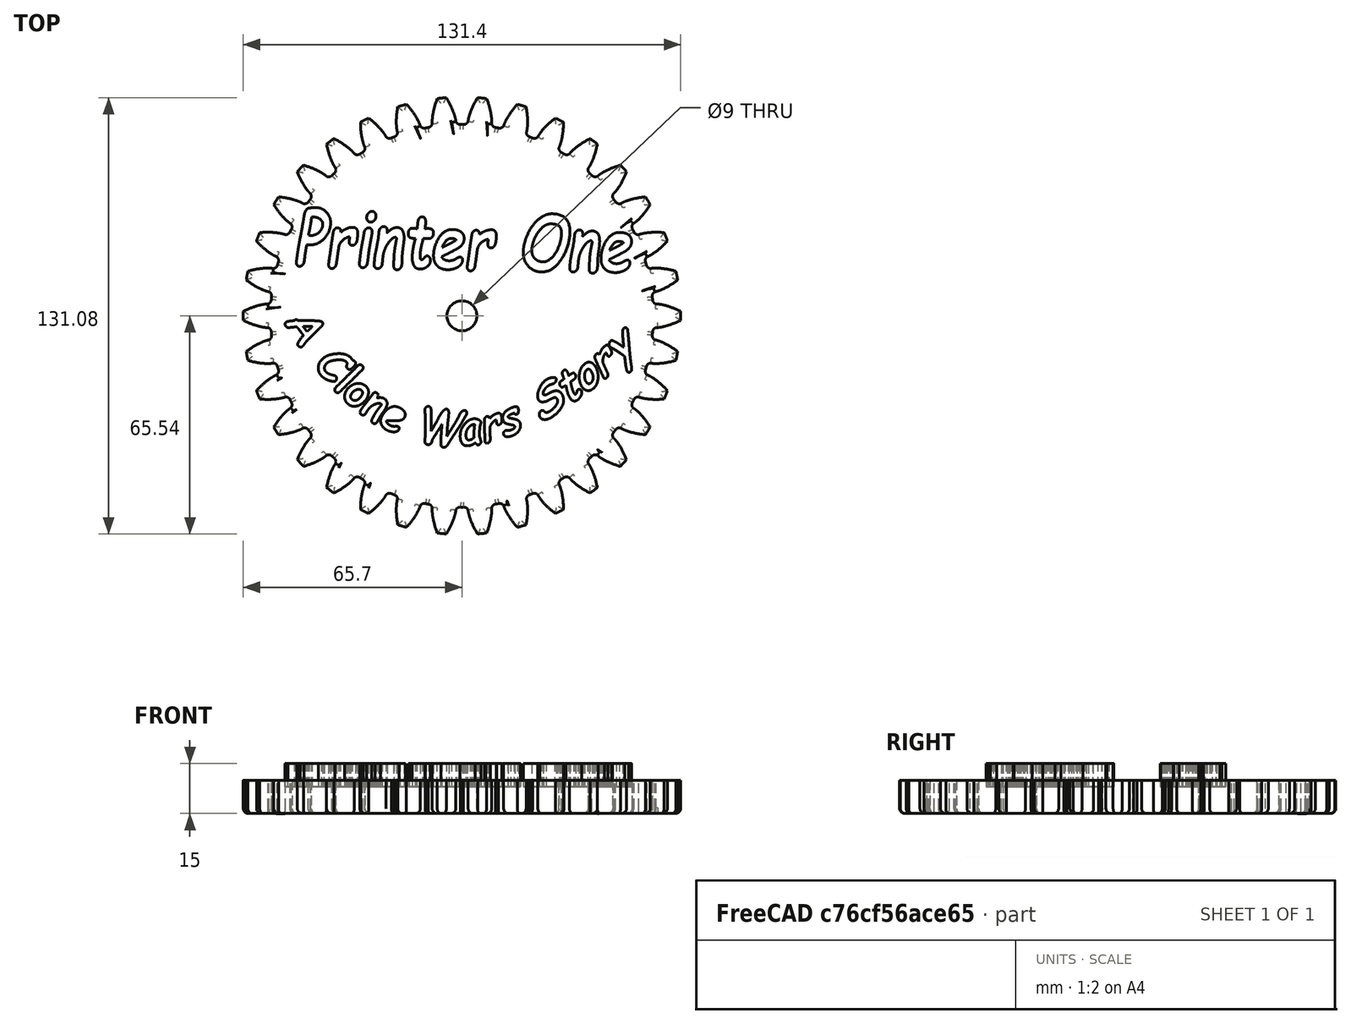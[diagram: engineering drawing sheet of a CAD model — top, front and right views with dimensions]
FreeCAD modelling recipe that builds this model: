
FCSTD DOCUMENT  (FreeCAD 0.16R6712 (Git))
Label: N34-Printer
License: All rights reserved
LicenseURL: http://en.wikipedia.org/wiki/All_rights_reserved
objects: Part::FeaturePython×2, Part::Part2DObjectPython×1, Part::Extrusion×1, Part::Cylinder×1, Part::Cut×1, Part::Fillet×1
note: 7 computed .brp shape members not serialized (recipe doc carries the construction recipe); baked Part::Feature solids carry a one-line shape summary decoded from their .brp

FEATURE [Part::Part2DObjectPython] InvoluteGear  # Draft 2D object (typed FeaturePython)
  ExternalGear = true
  HighPrecision = true
  MapMode = -1
  Modules = 3.65
  NumberOfTeeth = 34
  PressureAngle = 20
FEATURE [Part::Extrusion] Extrude001
  Base = -> InvoluteGear
  Dir = (0,0,1)
  Solid = true
FEATURE [Part::Cylinder] Cylinder  label="Cilindro"
  Angle = 360
  Height = 10
  Radius = 4.5
FEATURE [Part::Cut] Cut
  Base = -> Extrude001
  Tool = -> Cylinder
FEATURE [Part::Fillet] Fillet
  Base = -> Cut
  Edges = 273 edges r=1.5: [Edge3,Edge6,Edge9,Edge11,Edge12,Edge13,Edge14,Edge15,Edge16,Edge17,Edge18,Edge19,Edge20,Edge21,Edge22,Edge23,Edge24,Edge25,Edge26,Edge27,Edge28,Edge29,Edge30,Edge31,Edge32,Edge33,Edge34,Edge35,Edge36,Edge37,Edge38,Edge39,Edge40,Edge41,Edge42,Edge43,Edge44,Edge45,Edge46,Edge47,Edge48,Edge49,Edge50,+230 more]
FEATURE [Part::FeaturePython] Clone  label="Clone of Fusion"  # WARN: FeaturePython — macro-defined, semantics opaque (R4)
  Placement = pos=(-41,25,8) rot=(0,0,-1;0.017453rad)
  Scale = (0.6,0.75,7)
FEATURE [Part::FeaturePython] Clone001  label="Clone of Fusion001"  # WARN: FeaturePython — macro-defined, semantics opaque (R4)
  Placement = pos=(2,-23,8) rot=(0,0,-1;0.087266rad)
  Scale = (1.2,1.4,7)
